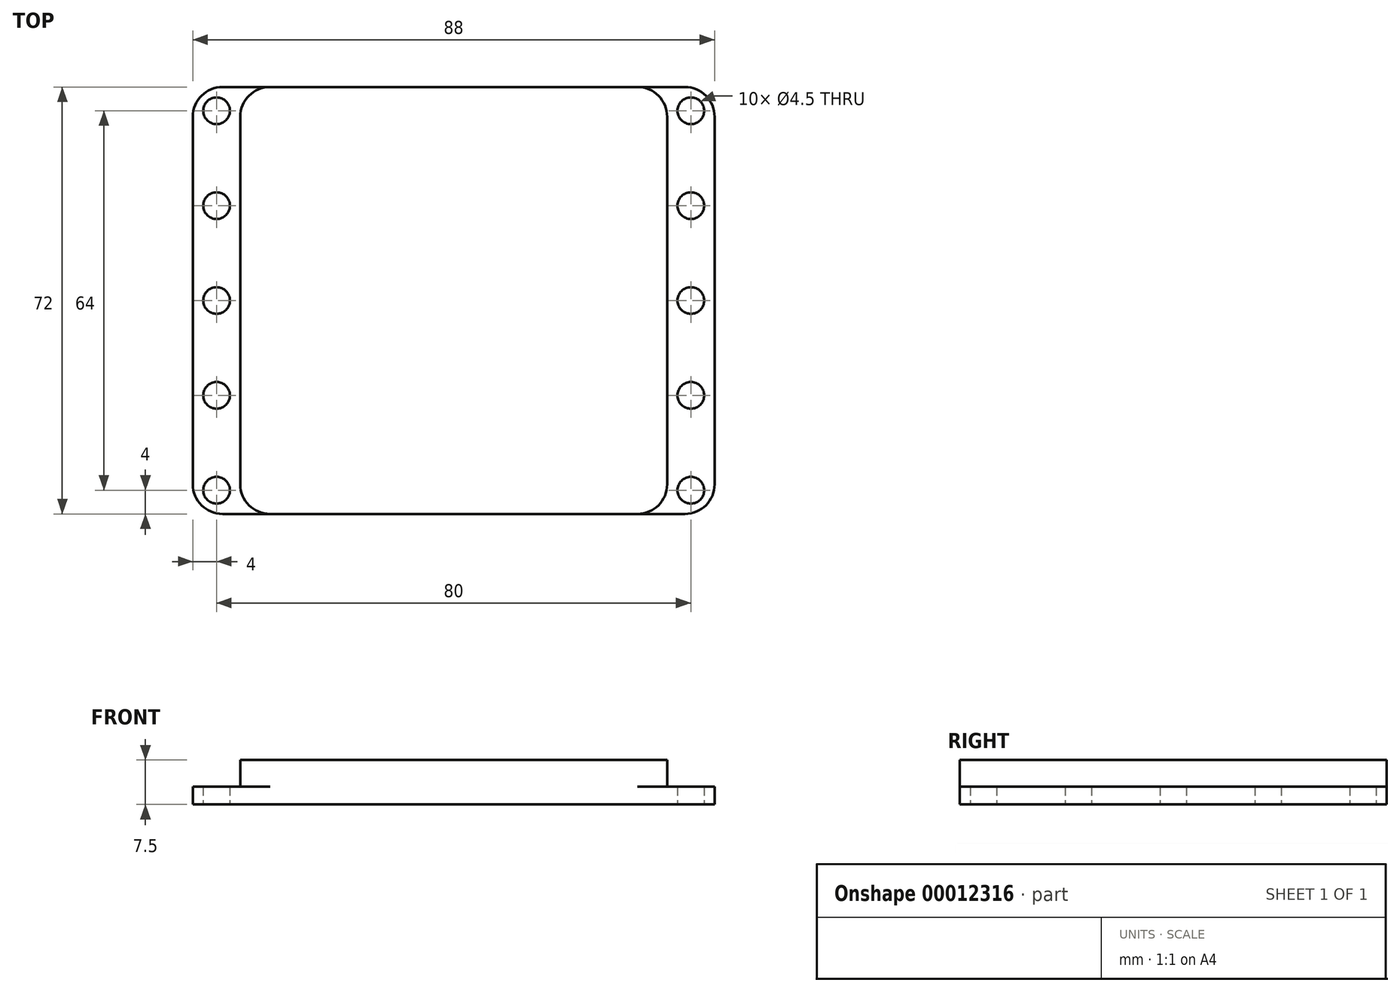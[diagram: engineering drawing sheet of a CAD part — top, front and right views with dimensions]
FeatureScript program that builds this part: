
annotation { "Feature Type Name" : "Feature", "Feature Type Description" : "" }
export const myFeature = defineFeature(function(context is Context, id is Id, definition is map)
    precondition{}
    {
        {
            var Q0;
            Q0=qCreatedBy(makeId("Front.planeOp"),FACE);
            var sketch = newSketch(context, id + "F0", { "sketchPlane" : qUnion([Q0])});
            skPoint(sketch, "E0.rect.middle", {"position": v(44, 3) * mm});
            skPoint(sketch, "E1.orphan", {"position": v(80, -1.5) * mm});
            skPoint(sketch, "E2.orphan", {"position": v(8, -1.5) * mm});
            skLineSegment(sketch, "E3.bottom", {"start": v(0, 0) * mm, "end": v(88, 0) * mm});
            skLineSegment(sketch, "E0.rect.bottom", {"start": v(80, 7.5) * mm, "end": v(8, 7.5) * mm});
            skLineSegment(sketch, "E4.trimOffspring", {"start": v(80, 3) * mm, "end": v(88, 3) * mm});
            skLineSegment(sketch, "E3.top", {"start": v(0, 3) * mm, "end": v(8, 3) * mm});
            skLineSegment(sketch, "E0.rect.left", {"start": v(80, 7.5) * mm, "end": v(80, 3) * mm});
            skLineSegment(sketch, "E3.left", {"start": v(0, 0) * mm, "end": v(0, 3) * mm});
            skLineSegment(sketch, "E3.right", {"start": v(88, 0) * mm, "end": v(88, 3) * mm});
            skLineSegment(sketch, "E0.rect.right", {"start": v(8, 7.5) * mm, "end": v(8, 3) * mm});
            skSolve(sketch);
        }
        {
            var Q0;
            Q0=makeQuery(id+"F0.imprint","IMPRINT",FACE,{"disambiguationData":[TD([[makeQuery(id+"F0.imprint","IMPRINT",EDGE,{"derivedFrom":sQuery(id+"F0.wireOp",EDGE,"E3.bottom")}),1.0]])]});
            extrude(context, id + "F1", {"entities" : qUnion([Q0]), "depth" : 72 * mm});
        }
        {
            var Q0;
            Q0=makeQuery(id+"F1.opExtrude","CAP_EDGE",EDGE,{"disambiguationData":[OSD([sQuery(id+"F0.wireOp",EDGE,"E0.rect.right")])],"isStart":false});
            var Q1;
            Q1=makeQuery(id+"F1.opExtrude","CAP_EDGE",EDGE,{"disambiguationData":[OSD([sQuery(id+"F0.wireOp",EDGE,"E0.rect.left")])],"isStart":false});
            var Q2;
            Q2=makeQuery(id+"F1.opExtrude","CAP_EDGE",EDGE,{"disambiguationData":[OSD([sQuery(id+"F0.wireOp",EDGE,"E0.rect.left")])],"isStart":true});
            var Q3;
            Q3=makeQuery(id+"F1.opExtrude","CAP_EDGE",EDGE,{"disambiguationData":[OSD([sQuery(id+"F0.wireOp",EDGE,"E0.rect.right")])],"isStart":true});
            var Q4;
            Q4=makeQuery(id+"F1.opExtrude","CAP_EDGE",EDGE,{"disambiguationData":[OSD([sQuery(id+"F0.wireOp",EDGE,"E3.right")])],"isStart":false});
            var Q5;
            Q5=makeQuery(id+"F1.opExtrude","CAP_EDGE",EDGE,{"disambiguationData":[OSD([sQuery(id+"F0.wireOp",EDGE,"E3.right")])],"isStart":true});
            var Q6;
            Q6=makeQuery(id+"F1.opExtrude","CAP_EDGE",EDGE,{"disambiguationData":[OSD([sQuery(id+"F0.wireOp",EDGE,"E3.left")])],"isStart":true});
            var Q7;
            Q7=makeQuery(id+"F1.opExtrude","CAP_EDGE",EDGE,{"disambiguationData":[OSD([sQuery(id+"F0.wireOp",EDGE,"E3.left")])],"isStart":false});
            fillet(context, id + "F2", {"entities" : qUnion([Q0, Q1, Q2, Q3, Q4, Q5, Q6, Q7]), "radius" : 5 * mm, "tangentPropagation" : true, "allowEdgeOverflow" : false});
        }
        {
            var Q0;
            Q0=makeQuery(id+"F1.opExtrude","SWEPT_FACE",FACE,{"disambiguationData":[OSD([sQuery(id+"F0.wireOp",EDGE,"E3.bottom")])]});
            var sketch = newSketch(context, id + "F3", { "sketchPlane" : qUnion([Q0])});
            skLineSegment(sketch, "E5.direction2", {"start": v(4, 68) * mm, "end": v(4, 52) * mm, "construction": true});
            skCircle(sketch, "E5.1.3.0", {"center": v(84, 20) * mm, "radius": 2.25 * mm});
            skCircle(sketch, "E5.1.4.0", {"center": v(84, 4) * mm, "radius": 2.25 * mm});
            skCircle(sketch, "E5.1.1.0", {"center": v(84, 52) * mm, "radius": 2.25 * mm});
            skCircle(sketch, "E5.1.2.0", {"center": v(84, 36) * mm, "radius": 2.25 * mm});
            skCircle(sketch, "E5.1.0.0", {"center": v(84, 68) * mm, "radius": 2.25 * mm});
            skLineSegment(sketch, "E5.direction1", {"start": v(4, 68) * mm, "end": v(84, 68) * mm, "construction": true});
            skCircle(sketch, "E5.0.4.0", {"center": v(4, 4) * mm, "radius": 2.25 * mm});
            skCircle(sketch, "E5.0.3.0", {"center": v(4, 20) * mm, "radius": 2.25 * mm});
            skCircle(sketch, "E5.0.2.0", {"center": v(4, 36) * mm, "radius": 2.25 * mm});
            skCircle(sketch, "E5.0.1.0", {"center": v(4, 52) * mm, "radius": 2.25 * mm});
            skCircle(sketch, "E6", {"center": v(4, 68) * mm, "radius": 2.25 * mm});
            skLineSegment(sketch, "E7", {"start": v(44, 72) * mm, "end": v(44, 0) * mm, "construction": true});
            skSolve(sketch);
        }
        {
            var Q0;
            Q0=qSketchRegion(id+"F3",true);
            extrude(context, id + "F4", {"entities" : qUnion([Q0]), "operationType" : NewBodyOperationType.REMOVE, "endBound" : BoundingType.UP_TO_NEXT, "oppositeDirection" : true, "depth" : 25 * mm});
        }
    });
